# Revit family: LNC
name_source: partatom
category: Lighting Fixtures
revit_build: Autodesk Revit Architecture 2012 (Build: 20110309_2315(x64)
units: mm (PartAtom-declared; Revit-internal decimal feet)

## types (5) — shared parameters
Apparent Load = 0 VA
Default Elevation = 48 "
Description = Typical mounting height is up to 12 feet with 40ft fixture spacing (without acrylic diffuser) and 30ft spacing with acrylic diffuser installed.
Glass = White Glass
Lamp = LED Lamp
Manufacturer = Hubbell outdoor Lighting
Manufacturer Fax = (866)-898-1065
Model = LNC
Product Documentation Link = http://www.hubbelloutdoor.com
Product Page URL = http://www.hubbelloutdoor.com
URL = http://www.hubbelloutdoor.com
Voltage = 120 V
Wattage Comments = 12-22 W

## per-type parameters (varying)
| type | Backbox | Photometric Web |
| Bronze | Metal - Hubbell - Bronze | Web LNC : LNC-7LU-5K-4, 7 LED, 5000K, TYPE 4 |
| Black | Metal - Hubbell - Black | Web LNC : LNC-5LU-3K-2, 5 LED, 3000K, TYPE 2 |
| Grey | Metal - Hubbell - Grey | Web LNC : LNC-5LU-3K-2, 5 LED, 3000K, TYPE 2 |
| Platinum | Metal - Hubbell - Platinum | Web LNC : LNC-5LU-3K-2, 5 LED, 3000K, TYPE 2 |
| White | Metal - Hubbell - White | Web LNC : LNC-5LU-3K-2, 5 LED, 3000K, TYPE 2 |

## geometry (parser evidence)
native form markers: Blend x11, Sweep x4
no freeform markers — native parametric forms only
